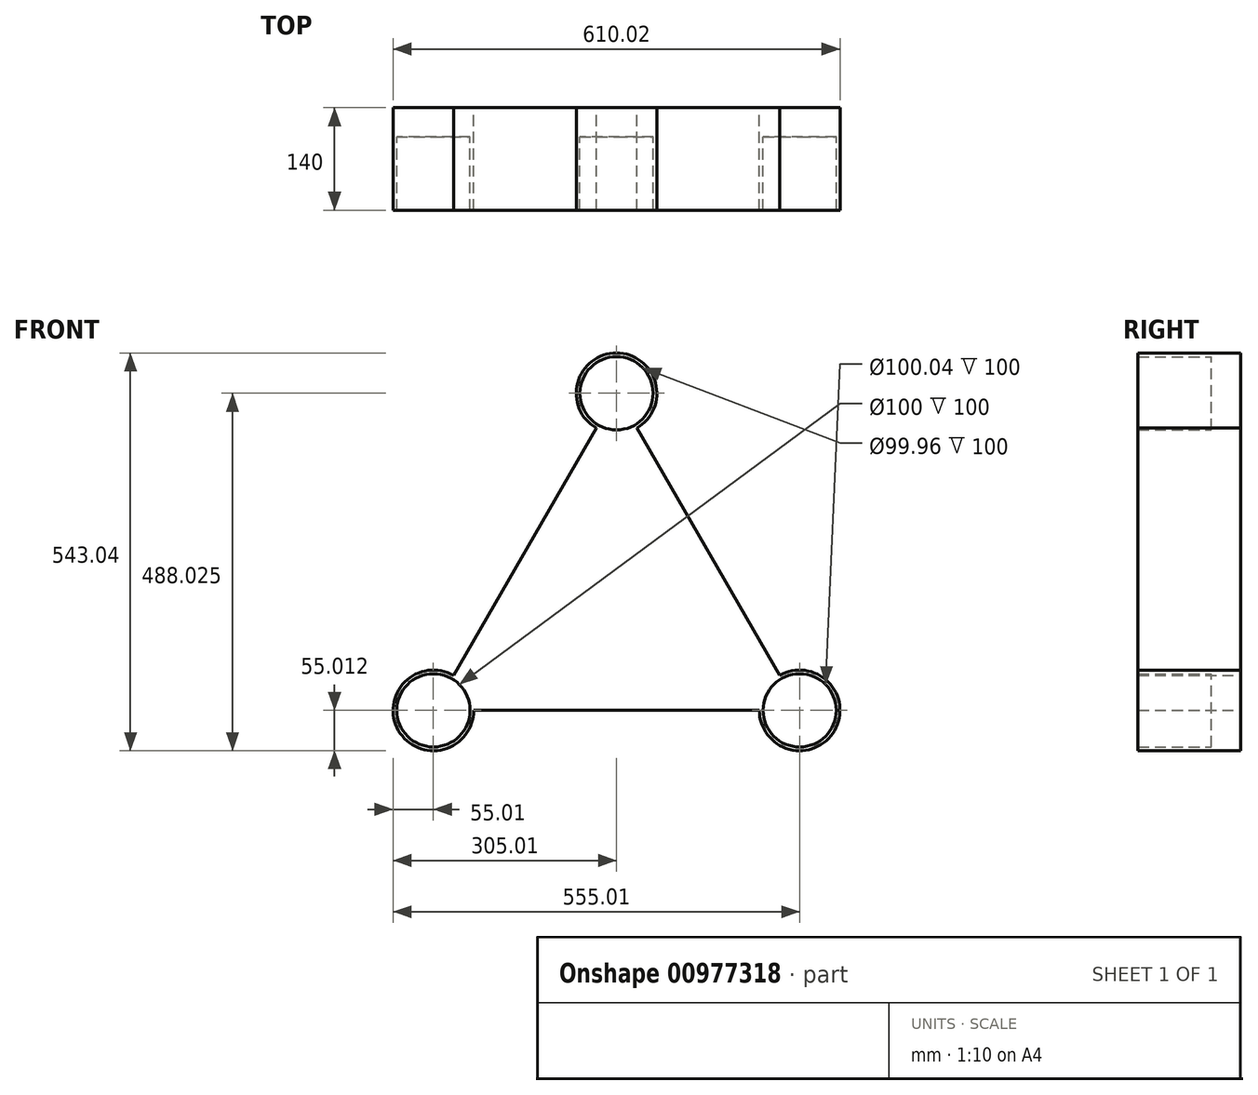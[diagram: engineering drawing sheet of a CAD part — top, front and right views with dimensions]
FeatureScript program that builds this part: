
annotation { "Feature Type Name" : "Feature", "Feature Type Description" : "" }
export const myFeature = defineFeature(function(context is Context, id is Id, definition is map)
    precondition{}
    {
        {
            var Q0;
            Q0=qCreatedBy(makeId("Front.planeOp"),FACE);
            var sketch = newSketch(context, id + "F0", { "sketchPlane" : qUnion([Q0])});
            skLineSegment(sketch, "E0", {"start": v(250, -144.34) * mm, "end": v(-250, -144.34) * mm});
            skLineSegment(sketch, "E1", {"start": v(-250, -144.34) * mm, "end": v(0, 288.68) * mm});
            skLineSegment(sketch, "E2", {"start": v(0, 288.68) * mm, "end": v(250, -144.34) * mm});
            skLineSegment(sketch, "E3", {"start": v(0, 288.68) * mm, "end": v(0, -144.34) * mm});
            skLineSegment(sketch, "E4", {"start": v(-125, 72.17) * mm, "end": v(250, -144.34) * mm});
            skLineSegment(sketch, "E5", {"start": v(-250, -144.34) * mm, "end": v(125, 72.17) * mm});
            skPoint(sketch, "E6", {"position": v(0, 0) * mm});
            skCircle(sketch, "E7", {"center": v(-250, -144.34) * mm, "radius": 50 * mm});
            skCircle(sketch, "E8", {"center": v(0, 288.68) * mm, "radius": 49.98 * mm});
            skCircle(sketch, "E9", {"center": v(250, -144.34) * mm, "radius": 50.02 * mm});
            skCircle(sketch, "E10", {"center": v(-250, -144.34) * mm, "radius": 55.01 * mm});
            skCircle(sketch, "E11", {"center": v(0, 288.68) * mm, "radius": 55.02 * mm});
            skCircle(sketch, "E12", {"center": v(250, -144.34) * mm, "radius": 55 * mm});
            skSolve(sketch);
        }
        {
            var Q0;
            {var subQ0=sQuery(id+"F0.wireOp",EDGE,"E10");var subQ1=sQuery(id+"F0.wireOp",EDGE,"E0");var subQ2=makeQuery(id+"F0.imprint","INTERSECT",VERTEX,{"derivedFrom":[subQ1,subQ0]});Q0=makeQuery(id+"F0.imprint","IMPRINT",FACE,{"disambiguationData":[TD([[makeQuery(id+"F0.imprint","IMPRINT",EDGE,{"disambiguationData":[TD([[subQ2,-1.0]])],"derivedFrom":subQ1}),1.0]])]});}
            var Q1;
            {var subQ0=sQuery(id+"F0.wireOp",EDGE,"E4");var subQ1=sQuery(id+"F0.wireOp",EDGE,"E1");var subQ2=makeQuery(id+"F0.imprint","INTERSECT",VERTEX,{"derivedFrom":[subQ1,subQ0]});Q1=makeQuery(id+"F0.imprint","IMPRINT",FACE,{"disambiguationData":[TD([[makeQuery(id+"F0.imprint","IMPRINT",EDGE,{"disambiguationData":[TD([[subQ2,1.0]])],"derivedFrom":subQ1}),-1.0]])]});}
            var Q2;
            {var subQ0=sQuery(id+"F0.wireOp",EDGE,"E3");var subQ1=sQuery(id+"F0.wireOp",EDGE,"E0");var subQ2=makeQuery(id+"F0.imprint","INTERSECT",VERTEX,{"derivedFrom":[subQ1,subQ0]});Q2=makeQuery(id+"F0.imprint","IMPRINT",FACE,{"disambiguationData":[TD([[makeQuery(id+"F0.imprint","IMPRINT",EDGE,{"disambiguationData":[TD([[subQ2,-1.0]])],"derivedFrom":subQ1}),-1.0]])]});}
            var Q3;
            {var subQ0=sQuery(id+"F0.wireOp",EDGE,"E10");var subQ1=sQuery(id+"F0.wireOp",EDGE,"E1");var subQ2=makeQuery(id+"F0.imprint","INTERSECT",VERTEX,{"derivedFrom":[subQ1,subQ0]});Q3=makeQuery(id+"F0.imprint","IMPRINT",FACE,{"disambiguationData":[TD([[makeQuery(id+"F0.imprint","IMPRINT",EDGE,{"disambiguationData":[TD([[subQ2,1.0]])],"derivedFrom":subQ1}),-1.0]])]});}
            var Q4;
            {var subQ0=sQuery(id+"F0.wireOp",EDGE,"E10");var subQ1=sQuery(id+"F0.wireOp",EDGE,"E0");var subQ2=makeQuery(id+"F0.imprint","INTERSECT",VERTEX,{"derivedFrom":[subQ1,subQ0]});Q4=makeQuery(id+"F0.imprint","IMPRINT",FACE,{"disambiguationData":[TD([[makeQuery(id+"F0.imprint","IMPRINT",EDGE,{"disambiguationData":[TD([[subQ2,-1.0]])],"derivedFrom":subQ1}),-1.0]])]});}
            var Q5;
            {var subQ0=sQuery(id+"F0.wireOp",EDGE,"E3");var subQ1=sQuery(id+"F0.wireOp",EDGE,"E0");var subQ2=makeQuery(id+"F0.imprint","INTERSECT",VERTEX,{"derivedFrom":[subQ1,subQ0]});Q5=makeQuery(id+"F0.imprint","IMPRINT",FACE,{"disambiguationData":[TD([[makeQuery(id+"F0.imprint","IMPRINT",EDGE,{"disambiguationData":[TD([[subQ2,1.0]])],"derivedFrom":subQ1}),-1.0]])]});}
            var Q6;
            {var subQ0=sQuery(id+"F0.wireOp",EDGE,"E5");var subQ1=sQuery(id+"F0.wireOp",EDGE,"E2");var subQ2=makeQuery(id+"F0.imprint","INTERSECT",VERTEX,{"derivedFrom":[subQ1,subQ0]});Q6=makeQuery(id+"F0.imprint","IMPRINT",FACE,{"disambiguationData":[TD([[makeQuery(id+"F0.imprint","IMPRINT",EDGE,{"disambiguationData":[TD([[subQ2,-1.0]])],"derivedFrom":subQ1}),-1.0]])]});}
            var Q7;
            {var subQ0=sQuery(id+"F0.wireOp",EDGE,"E5");var subQ1=sQuery(id+"F0.wireOp",EDGE,"E2");var subQ2=makeQuery(id+"F0.imprint","INTERSECT",VERTEX,{"derivedFrom":[subQ1,subQ0]});Q7=makeQuery(id+"F0.imprint","IMPRINT",FACE,{"disambiguationData":[TD([[makeQuery(id+"F0.imprint","IMPRINT",EDGE,{"disambiguationData":[TD([[subQ2,1.0]])],"derivedFrom":subQ1}),-1.0]])]});}
            var Q8;
            {var subQ0=sQuery(id+"F0.wireOp",EDGE,"E12");var subQ1=sQuery(id+"F0.wireOp",EDGE,"E2");var subQ2=makeQuery(id+"F0.imprint","INTERSECT",VERTEX,{"derivedFrom":[subQ1,subQ0]});Q8=makeQuery(id+"F0.imprint","IMPRINT",FACE,{"disambiguationData":[TD([[makeQuery(id+"F0.imprint","IMPRINT",EDGE,{"disambiguationData":[TD([[subQ2,-1.0]])],"derivedFrom":subQ1}),-1.0]])]});}
            var Q9;
            {var subQ0=sQuery(id+"F0.wireOp",EDGE,"E12");var subQ1=sQuery(id+"F0.wireOp",EDGE,"E0");var subQ2=makeQuery(id+"F0.imprint","INTERSECT",VERTEX,{"derivedFrom":[subQ1,subQ0]});Q9=makeQuery(id+"F0.imprint","IMPRINT",FACE,{"disambiguationData":[TD([[makeQuery(id+"F0.imprint","IMPRINT",EDGE,{"disambiguationData":[TD([[subQ2,1.0]])],"derivedFrom":subQ1}),-1.0]])]});}
            var Q10;
            {var subQ0=sQuery(id+"F0.wireOp",EDGE,"E12");var subQ1=sQuery(id+"F0.wireOp",EDGE,"E0");var subQ2=makeQuery(id+"F0.imprint","INTERSECT",VERTEX,{"derivedFrom":[subQ1,subQ0]});Q10=makeQuery(id+"F0.imprint","IMPRINT",FACE,{"disambiguationData":[TD([[makeQuery(id+"F0.imprint","IMPRINT",EDGE,{"disambiguationData":[TD([[subQ2,1.0]])],"derivedFrom":subQ1}),1.0]])]});}
            var Q11;
            {var subQ0=sQuery(id+"F0.wireOp",EDGE,"E4");var subQ1=sQuery(id+"F0.wireOp",EDGE,"E1");var subQ2=makeQuery(id+"F0.imprint","INTERSECT",VERTEX,{"derivedFrom":[subQ1,subQ0]});Q11=makeQuery(id+"F0.imprint","IMPRINT",FACE,{"disambiguationData":[TD([[makeQuery(id+"F0.imprint","IMPRINT",EDGE,{"disambiguationData":[TD([[subQ2,-1.0]])],"derivedFrom":subQ1}),-1.0]])]});}
            var Q12;
            {var subQ0=sQuery(id+"F0.wireOp",EDGE,"E11");var subQ1=sQuery(id+"F0.wireOp",EDGE,"E1");var subQ2=makeQuery(id+"F0.imprint","INTERSECT",VERTEX,{"derivedFrom":[subQ1,subQ0]});Q12=makeQuery(id+"F0.imprint","IMPRINT",FACE,{"disambiguationData":[TD([[makeQuery(id+"F0.imprint","IMPRINT",EDGE,{"disambiguationData":[TD([[subQ2,-1.0]])],"derivedFrom":subQ1}),1.0]])]});}
            var Q13;
            {var subQ0=sQuery(id+"F0.wireOp",EDGE,"E11");var subQ1=sQuery(id+"F0.wireOp",EDGE,"E2");var subQ2=makeQuery(id+"F0.imprint","INTERSECT",VERTEX,{"derivedFrom":[subQ1,subQ0]});Q13=makeQuery(id+"F0.imprint","IMPRINT",FACE,{"disambiguationData":[TD([[makeQuery(id+"F0.imprint","IMPRINT",EDGE,{"disambiguationData":[TD([[subQ2,1.0]])],"derivedFrom":subQ1}),-1.0]])]});}
            var Q14;
            {var subQ0=sQuery(id+"F0.wireOp",EDGE,"E11");var subQ1=sQuery(id+"F0.wireOp",EDGE,"E1");var subQ2=makeQuery(id+"F0.imprint","INTERSECT",VERTEX,{"derivedFrom":[subQ1,subQ0]});Q14=makeQuery(id+"F0.imprint","IMPRINT",FACE,{"disambiguationData":[TD([[makeQuery(id+"F0.imprint","IMPRINT",EDGE,{"disambiguationData":[TD([[subQ2,-1.0]])],"derivedFrom":subQ1}),-1.0]])]});}
            extrude(context, id + "F1", {"entities" : qUnion([Q0, Q1, Q2, Q3, Q4, Q5, Q6, Q7, Q8, Q9, Q10, Q11, Q12, Q13, Q14]), "depth" : 100 * mm, "offsetDistance" : 25 * mm});
        }
        {
            var Q0;
            {var subQ1=sQuery(id+"F0.wireOp",EDGE,"E1");var subQ3=sQuery(id+"F0.wireOp",EDGE,"E8");var subQ4=makeQuery(id+"F0.imprint","INTERSECT",VERTEX,{"derivedFrom":[subQ1,subQ3]});Q0=makeQuery(id+"F0.imprint","IMPRINT",FACE,{"disambiguationData":[TD([[makeQuery(id+"F0.imprint","IMPRINT",EDGE,{"disambiguationData":[TD([[subQ4,1.0]])],"derivedFrom":subQ3}),1.0]])]});}
            var Q1;
            {var subQ0=sQuery(id+"F0.wireOp",EDGE,"E5");var subQ1=sQuery(id+"F0.wireOp",EDGE,"E2");var subQ2=makeQuery(id+"F0.imprint","INTERSECT",VERTEX,{"derivedFrom":[subQ1,subQ0]});Q1=makeQuery(id+"F0.imprint","IMPRINT",FACE,{"disambiguationData":[TD([[makeQuery(id+"F0.imprint","IMPRINT",EDGE,{"disambiguationData":[TD([[subQ2,1.0]])],"derivedFrom":subQ1}),-1.0]])]});}
            var Q2;
            {var subQ0=sQuery(id+"F0.wireOp",EDGE,"E4");var subQ1=sQuery(id+"F0.wireOp",EDGE,"E1");var subQ2=makeQuery(id+"F0.imprint","INTERSECT",VERTEX,{"derivedFrom":[subQ1,subQ0]});Q2=makeQuery(id+"F0.imprint","IMPRINT",FACE,{"disambiguationData":[TD([[makeQuery(id+"F0.imprint","IMPRINT",EDGE,{"disambiguationData":[TD([[subQ2,-1.0]])],"derivedFrom":subQ1}),-1.0]])]});}
            var Q3;
            {var subQ1=sQuery(id+"F0.wireOp",EDGE,"E1");var subQ3=sQuery(id+"F0.wireOp",EDGE,"E8");var subQ4=makeQuery(id+"F0.imprint","INTERSECT",VERTEX,{"derivedFrom":[subQ1,subQ3]});Q3=makeQuery(id+"F0.imprint","IMPRINT",FACE,{"disambiguationData":[TD([[makeQuery(id+"F0.imprint","IMPRINT",EDGE,{"disambiguationData":[TD([[subQ4,-1.0]])],"derivedFrom":subQ3}),1.0]])]});}
            var Q4;
            {var subQ1=sQuery(id+"F0.wireOp",EDGE,"E2");var subQ3=sQuery(id+"F0.wireOp",EDGE,"E8");var subQ4=makeQuery(id+"F0.imprint","INTERSECT",VERTEX,{"derivedFrom":[subQ1,subQ3]});Q4=makeQuery(id+"F0.imprint","IMPRINT",FACE,{"disambiguationData":[TD([[makeQuery(id+"F0.imprint","IMPRINT",EDGE,{"disambiguationData":[TD([[subQ4,1.0]])],"derivedFrom":subQ3}),1.0]])]});}
            var Q5;
            {var subQ0=sQuery(id+"F0.wireOp",EDGE,"E11");var subQ1=sQuery(id+"F0.wireOp",EDGE,"E2");var subQ2=makeQuery(id+"F0.imprint","INTERSECT",VERTEX,{"derivedFrom":[subQ1,subQ0]});Q5=makeQuery(id+"F0.imprint","IMPRINT",FACE,{"disambiguationData":[TD([[makeQuery(id+"F0.imprint","IMPRINT",EDGE,{"disambiguationData":[TD([[subQ2,1.0]])],"derivedFrom":subQ1}),-1.0]])]});}
            var Q6;
            {var subQ0=sQuery(id+"F0.wireOp",EDGE,"E11");var subQ1=sQuery(id+"F0.wireOp",EDGE,"E1");var subQ2=makeQuery(id+"F0.imprint","INTERSECT",VERTEX,{"derivedFrom":[subQ1,subQ0]});Q6=makeQuery(id+"F0.imprint","IMPRINT",FACE,{"disambiguationData":[TD([[makeQuery(id+"F0.imprint","IMPRINT",EDGE,{"disambiguationData":[TD([[subQ2,-1.0]])],"derivedFrom":subQ1}),-1.0]])]});}
            var Q7;
            {var subQ0=sQuery(id+"F0.wireOp",EDGE,"E11");var subQ1=sQuery(id+"F0.wireOp",EDGE,"E1");var subQ2=makeQuery(id+"F0.imprint","INTERSECT",VERTEX,{"derivedFrom":[subQ1,subQ0]});Q7=makeQuery(id+"F0.imprint","IMPRINT",FACE,{"disambiguationData":[TD([[makeQuery(id+"F0.imprint","IMPRINT",EDGE,{"disambiguationData":[TD([[subQ2,-1.0]])],"derivedFrom":subQ1}),1.0]])]});}
            var Q8;
            {var subQ0=sQuery(id+"F0.wireOp",EDGE,"E4");var subQ1=sQuery(id+"F0.wireOp",EDGE,"E1");var subQ2=makeQuery(id+"F0.imprint","INTERSECT",VERTEX,{"derivedFrom":[subQ1,subQ0]});Q8=makeQuery(id+"F0.imprint","IMPRINT",FACE,{"disambiguationData":[TD([[makeQuery(id+"F0.imprint","IMPRINT",EDGE,{"disambiguationData":[TD([[subQ2,1.0]])],"derivedFrom":subQ1}),-1.0]])]});}
            var Q9;
            {var subQ0=sQuery(id+"F0.wireOp",EDGE,"E3");var subQ1=sQuery(id+"F0.wireOp",EDGE,"E0");var subQ2=makeQuery(id+"F0.imprint","INTERSECT",VERTEX,{"derivedFrom":[subQ1,subQ0]});Q9=makeQuery(id+"F0.imprint","IMPRINT",FACE,{"disambiguationData":[TD([[makeQuery(id+"F0.imprint","IMPRINT",EDGE,{"disambiguationData":[TD([[subQ2,-1.0]])],"derivedFrom":subQ1}),-1.0]])]});}
            var Q10;
            {var subQ0=sQuery(id+"F0.wireOp",EDGE,"E3");var subQ1=sQuery(id+"F0.wireOp",EDGE,"E0");var subQ2=makeQuery(id+"F0.imprint","INTERSECT",VERTEX,{"derivedFrom":[subQ1,subQ0]});Q10=makeQuery(id+"F0.imprint","IMPRINT",FACE,{"disambiguationData":[TD([[makeQuery(id+"F0.imprint","IMPRINT",EDGE,{"disambiguationData":[TD([[subQ2,1.0]])],"derivedFrom":subQ1}),-1.0]])]});}
            var Q11;
            {var subQ0=sQuery(id+"F0.wireOp",EDGE,"E5");var subQ1=sQuery(id+"F0.wireOp",EDGE,"E2");var subQ2=makeQuery(id+"F0.imprint","INTERSECT",VERTEX,{"derivedFrom":[subQ1,subQ0]});Q11=makeQuery(id+"F0.imprint","IMPRINT",FACE,{"disambiguationData":[TD([[makeQuery(id+"F0.imprint","IMPRINT",EDGE,{"disambiguationData":[TD([[subQ2,-1.0]])],"derivedFrom":subQ1}),-1.0]])]});}
            var Q12;
            {var subQ1=sQuery(id+"F0.wireOp",EDGE,"E2");var subQ3=sQuery(id+"F0.wireOp",EDGE,"E9");var subQ4=makeQuery(id+"F0.imprint","INTERSECT",VERTEX,{"derivedFrom":[subQ1,subQ3]});Q12=makeQuery(id+"F0.imprint","IMPRINT",FACE,{"disambiguationData":[TD([[makeQuery(id+"F0.imprint","IMPRINT",EDGE,{"disambiguationData":[TD([[subQ4,-1.0]])],"derivedFrom":subQ3}),1.0]])]});}
            var Q13;
            {var subQ1=sQuery(id+"F0.wireOp",EDGE,"E0");var subQ3=sQuery(id+"F0.wireOp",EDGE,"E9");var subQ4=makeQuery(id+"F0.imprint","INTERSECT",VERTEX,{"derivedFrom":[subQ1,subQ3]});Q13=makeQuery(id+"F0.imprint","IMPRINT",FACE,{"disambiguationData":[TD([[makeQuery(id+"F0.imprint","IMPRINT",EDGE,{"disambiguationData":[TD([[subQ4,-1.0]])],"derivedFrom":subQ3}),1.0]])]});}
            var Q14;
            {var subQ0=sQuery(id+"F0.wireOp",EDGE,"E12");var subQ1=sQuery(id+"F0.wireOp",EDGE,"E0");var subQ2=makeQuery(id+"F0.imprint","INTERSECT",VERTEX,{"derivedFrom":[subQ1,subQ0]});Q14=makeQuery(id+"F0.imprint","IMPRINT",FACE,{"disambiguationData":[TD([[makeQuery(id+"F0.imprint","IMPRINT",EDGE,{"disambiguationData":[TD([[subQ2,1.0]])],"derivedFrom":subQ1}),1.0]])]});}
            var Q15;
            {var subQ0=sQuery(id+"F0.wireOp",EDGE,"E12");var subQ1=sQuery(id+"F0.wireOp",EDGE,"E2");var subQ2=makeQuery(id+"F0.imprint","INTERSECT",VERTEX,{"derivedFrom":[subQ1,subQ0]});Q15=makeQuery(id+"F0.imprint","IMPRINT",FACE,{"disambiguationData":[TD([[makeQuery(id+"F0.imprint","IMPRINT",EDGE,{"disambiguationData":[TD([[subQ2,-1.0]])],"derivedFrom":subQ1}),-1.0]])]});}
            var Q16;
            {var subQ0=sQuery(id+"F0.wireOp",EDGE,"E12");var subQ1=sQuery(id+"F0.wireOp",EDGE,"E0");var subQ2=makeQuery(id+"F0.imprint","INTERSECT",VERTEX,{"derivedFrom":[subQ1,subQ0]});Q16=makeQuery(id+"F0.imprint","IMPRINT",FACE,{"disambiguationData":[TD([[makeQuery(id+"F0.imprint","IMPRINT",EDGE,{"disambiguationData":[TD([[subQ2,1.0]])],"derivedFrom":subQ1}),-1.0]])]});}
            var Q17;
            {var subQ1=sQuery(id+"F0.wireOp",EDGE,"E0");var subQ3=sQuery(id+"F0.wireOp",EDGE,"E9");var subQ4=makeQuery(id+"F0.imprint","INTERSECT",VERTEX,{"derivedFrom":[subQ1,subQ3]});Q17=makeQuery(id+"F0.imprint","IMPRINT",FACE,{"disambiguationData":[TD([[makeQuery(id+"F0.imprint","IMPRINT",EDGE,{"disambiguationData":[TD([[subQ4,1.0]])],"derivedFrom":subQ3}),1.0]])]});}
            var Q18;
            {var subQ1=sQuery(id+"F0.wireOp",EDGE,"E1");var subQ3=sQuery(id+"F0.wireOp",EDGE,"E7");var subQ4=makeQuery(id+"F0.imprint","INTERSECT",VERTEX,{"derivedFrom":[subQ1,subQ3]});Q18=makeQuery(id+"F0.imprint","IMPRINT",FACE,{"disambiguationData":[TD([[makeQuery(id+"F0.imprint","IMPRINT",EDGE,{"disambiguationData":[TD([[subQ4,1.0]])],"derivedFrom":subQ3}),1.0]])]});}
            var Q19;
            {var subQ0=sQuery(id+"F0.wireOp",EDGE,"E10");var subQ1=sQuery(id+"F0.wireOp",EDGE,"E1");var subQ2=makeQuery(id+"F0.imprint","INTERSECT",VERTEX,{"derivedFrom":[subQ1,subQ0]});Q19=makeQuery(id+"F0.imprint","IMPRINT",FACE,{"disambiguationData":[TD([[makeQuery(id+"F0.imprint","IMPRINT",EDGE,{"disambiguationData":[TD([[subQ2,1.0]])],"derivedFrom":subQ1}),-1.0]])]});}
            var Q20;
            {var subQ0=sQuery(id+"F0.wireOp",EDGE,"E10");var subQ1=sQuery(id+"F0.wireOp",EDGE,"E0");var subQ2=makeQuery(id+"F0.imprint","INTERSECT",VERTEX,{"derivedFrom":[subQ1,subQ0]});Q20=makeQuery(id+"F0.imprint","IMPRINT",FACE,{"disambiguationData":[TD([[makeQuery(id+"F0.imprint","IMPRINT",EDGE,{"disambiguationData":[TD([[subQ2,-1.0]])],"derivedFrom":subQ1}),1.0]])]});}
            var Q21;
            {var subQ1=sQuery(id+"F0.wireOp",EDGE,"E0");var subQ3=sQuery(id+"F0.wireOp",EDGE,"E7");var subQ4=makeQuery(id+"F0.imprint","INTERSECT",VERTEX,{"derivedFrom":[subQ1,subQ3]});Q21=makeQuery(id+"F0.imprint","IMPRINT",FACE,{"disambiguationData":[TD([[makeQuery(id+"F0.imprint","IMPRINT",EDGE,{"disambiguationData":[TD([[subQ4,1.0]])],"derivedFrom":subQ3}),1.0]])]});}
            var Q22;
            {var subQ1=sQuery(id+"F0.wireOp",EDGE,"E0");var subQ3=sQuery(id+"F0.wireOp",EDGE,"E7");var subQ4=makeQuery(id+"F0.imprint","INTERSECT",VERTEX,{"derivedFrom":[subQ1,subQ3]});Q22=makeQuery(id+"F0.imprint","IMPRINT",FACE,{"disambiguationData":[TD([[makeQuery(id+"F0.imprint","IMPRINT",EDGE,{"disambiguationData":[TD([[subQ4,-1.0]])],"derivedFrom":subQ3}),1.0]])]});}
            var Q23;
            {var subQ0=sQuery(id+"F0.wireOp",EDGE,"E10");var subQ1=sQuery(id+"F0.wireOp",EDGE,"E0");var subQ2=makeQuery(id+"F0.imprint","INTERSECT",VERTEX,{"derivedFrom":[subQ1,subQ0]});Q23=makeQuery(id+"F0.imprint","IMPRINT",FACE,{"disambiguationData":[TD([[makeQuery(id+"F0.imprint","IMPRINT",EDGE,{"disambiguationData":[TD([[subQ2,-1.0]])],"derivedFrom":subQ1}),-1.0]])]});}
            extrude(context, id + "F2", {"entities" : qUnion([Q0, Q1, Q2, Q3, Q4, Q5, Q6, Q7, Q8, Q9, Q10, Q11, Q12, Q13, Q14, Q15, Q16, Q17, Q18, Q19, Q20, Q21, Q22, Q23]), "operationType" : NewBodyOperationType.ADD, "oppositeDirection" : true, "depth" : 40 * mm, "offsetDistance" : 25 * mm});
        }
    });
